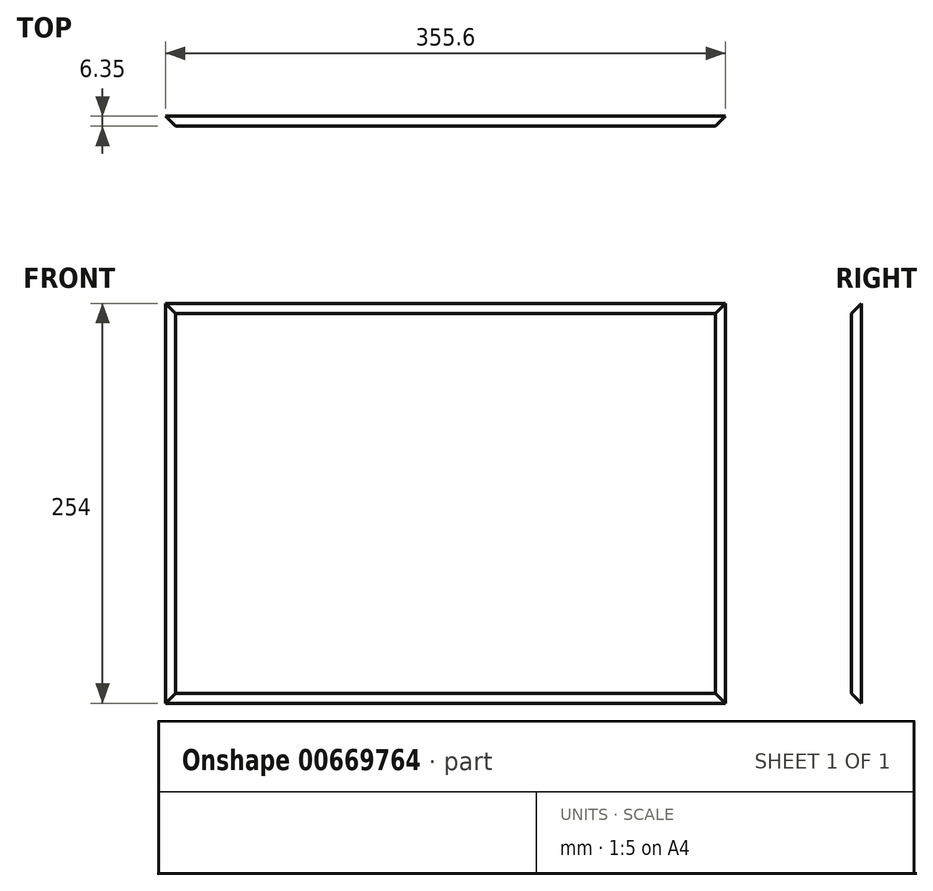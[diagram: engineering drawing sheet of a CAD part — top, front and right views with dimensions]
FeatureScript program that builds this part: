
annotation { "Feature Type Name" : "Feature", "Feature Type Description" : "" }
export const myFeature = defineFeature(function(context is Context, id is Id, definition is map)
    precondition{}
    {
        {
            var Q0;
            Q0=qCreatedBy(makeId("Front.planeOp"),FACE);
            var sketch = newSketch(context, id + "F0", { "sketchPlane" : qUnion([Q0])});
            skLineSegment(sketch, "E0.bottom", {"start": v(-181.1, 133.36) * mm, "end": v(174.5, 133.36) * mm});
            skLineSegment(sketch, "E0.top", {"start": v(-181.1, -120.64) * mm, "end": v(174.5, -120.64) * mm});
            skLineSegment(sketch, "E0.left", {"start": v(-181.1, 133.36) * mm, "end": v(-181.1, -120.64) * mm});
            skLineSegment(sketch, "E0.right", {"start": v(174.5, 133.36) * mm, "end": v(174.5, -120.64) * mm});
            skSolve(sketch);
        }
        {
            var Q0;
            Q0 = qSketchRegion(id + "F0", true);
            extrude(context, id + "F1", {"entities" : qUnion([Q0]), "depth" : 6.35 * mm, "offsetDistance" : 25.4 * mm});
        }
        {
            var Q0;
            Q0=makeQuery(id+"F1.opExtrude","CAP_FACE",FACE,{"disambiguationData":[OSD([sQuery(id+"F0.wireOp",EDGE,"E0.bottom"),sQuery(id+"F0.wireOp",EDGE,"E0.top"),sQuery(id+"F0.wireOp",EDGE,"E0.left"),sQuery(id+"F0.wireOp",EDGE,"E0.right")])],"isStart":false});
            chamfer(context, id + "F2", {"entities" : qUnion([Q0]), "chamferType" : ChamferType.OFFSET_ANGLE, "width" : 6.35 * mm, "oppositeDirection" : false, "angle" : 45 * degree, "tangentPropagation" : true});
        }
    });
